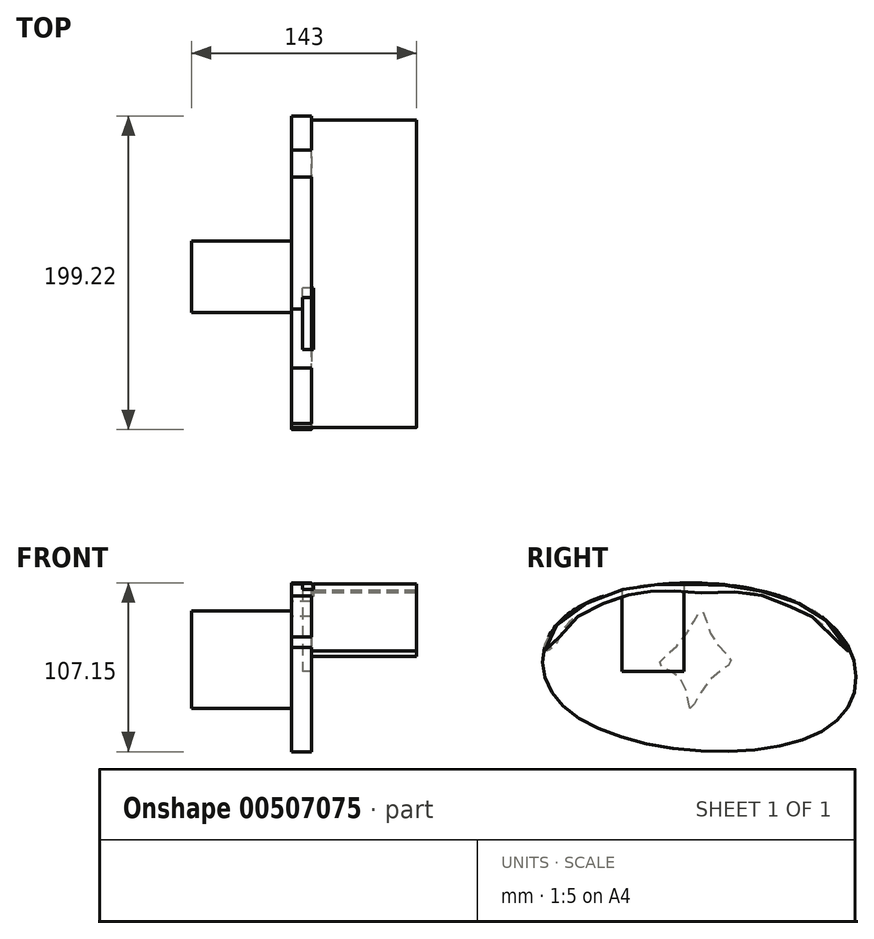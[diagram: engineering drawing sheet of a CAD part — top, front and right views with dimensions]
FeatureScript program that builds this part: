
annotation { "Feature Type Name" : "Feature", "Feature Type Description" : "" }
export const myFeature = defineFeature(function(context is Context, id is Id, definition is map)
    precondition{}
    {
        {
            var Q0;
            Q0=qCreatedBy(makeId("Right.planeOp"),FACE);
            var sketch = newSketch(context, id + "F0", { "sketchPlane" : qUnion([Q0])});
            skFitSpline(sketch, "E0", {"points": [v(-52.26, 26.74) * mm, v(-52.02, -34.24) * mm, v(116.31, -42.83) * mm, v(110.35, 24.54) * mm, v(-52.26, 26.74) * mm]});
            skSolve(sketch);
        }
        {
            var Q0;
            Q0=makeQuery(id+"F0.imprint","IMPRINT",FACE,{"disambiguationData":[TD([[makeQuery(id+"F0.imprint","IMPRINT",EDGE,{"derivedFrom":sQuery(id+"F0.wireOp",EDGE,"E0")}),1.0]])]});
            extrude(context, id + "F1", {"entities" : qUnion([Q0]), "depth" : 12.7 * mm});
        }
        {
            var Q0;
            Q0=qCreatedBy(makeId("Right.planeOp"),FACE);
            var sketch = newSketch(context, id + "F2", { "sketchPlane" : qUnion([Q0])});
            skFitSpline(sketch, "E1", {"points": [v(25.54, -32.86) * mm, v(20.23, -14.93) * mm, v(6.03, -4.9) * mm, v(20.25, 9.96) * mm, v(32.93, 29) * mm, v(40.33, 11.1) * mm, v(51.59, -3.17) * mm, v(38.82, -14.11) * mm, v(25.54, -32.86) * mm]});
            skSolve(sketch);
        }
        {
            var Q0;
            Q0=makeQuery(id+"F2.imprint","IMPRINT",FACE,{"disambiguationData":[TD([[makeQuery(id+"F2.imprint","IMPRINT",EDGE,{"derivedFrom":sQuery(id+"F2.wireOp",EDGE,"E1")}),-1.0]])]});
            extrude(context, id + "F3", {"entities" : qUnion([Q0]), "operationType" : NewBodyOperationType.ADD, "oppositeDirection" : true, "depth" : 63.75 * mm});
        }
        {
            var Q0;
            Q0=qCreatedBy(makeId("Top.planeOp"),FACE);
            var sketch = newSketch(context, id + "F4", { "sketchPlane" : qUnion([Q0])});
            skArc(sketch, "E2", {"start": v(13.62, -67.46) * mm, "mid": v(81.56, 31.79) * mm, "end": v(13.16, 130.71) * mm});
            skSolve(sketch);
        }
        {
            var Q0;
            Q0=sQuery(id+"F4.wireOp",EDGE,"E2");
            extrude(context, id + "F5", {"bodyType" : ToolBodyType.SURFACE, "surfaceEntities" : qUnion([Q0]), "oppositeDirection" : true, "depth" : 16 * mm});
        }
        {
            var Q0;
            Q0=qCreatedBy(makeId("Right.planeOp"),FACE);
            var sketch = newSketch(context, id + "F6", { "sketchPlane" : qUnion([Q0])});
            skFitSpline(sketch, "E3", {"points": [v(-66.68, 3.98) * mm, v(-60.7, 18) * mm, v(-37.08, 35.13) * mm, v(-7.37, 44.85) * mm, v(16.95, 45.89) * mm, v(41.56, 45.49) * mm, v(68.88, 41.75) * mm, v(98.43, 32.2) * mm, v(115.66, 18.57) * mm, v(128.15, 0) * mm, v(111.03, 18.78) * mm, v(96.84, 28.7) * mm, v(82.82, 34.34) * mm, v(63.83, 40.55) * mm, v(47.76, 40.57) * mm, v(23.87, 40.93) * mm, v(12.48, 41.8) * mm, v(0, 41.25) * mm, v(-10.09, 39.97) * mm, v(-24.19, 35.97) * mm, v(-38.05, 29.46) * mm, v(-53.49, 19.45) * mm, v(-60.85, 6.58) * mm, v(-66.68, 3.98) * mm]});
            skSolve(sketch);
        }
        {
            var Q0;
            Q0 = qSketchRegion(id + "F6", true);
            extrude(context, id + "F7", {"entities" : qUnion([Q0]), "operationType" : NewBodyOperationType.ADD, "depth" : 79.25 * mm});
        }
        {
            var Q0;
            Q0=qCreatedBy(makeId("Right.planeOp"),FACE);
            var sketch = newSketch(context, id + "F8", { "sketchPlane" : qUnion([Q0])});
            skLineSegment(sketch, "E4.bottom", {"start": v(-17.58, 46.45) * mm, "end": v(21.52, 46.45) * mm});
            skLineSegment(sketch, "E4.top", {"start": v(-17.58, -9.33) * mm, "end": v(21.52, -9.33) * mm});
            skLineSegment(sketch, "E4.left", {"start": v(-17.58, 46.45) * mm, "end": v(-17.58, -9.33) * mm});
            skLineSegment(sketch, "E4.right", {"start": v(21.52, 46.45) * mm, "end": v(21.52, -9.33) * mm});
            skSolve(sketch);
        }
        {
            var Q0;
            Q0 = qSketchRegion(id + "F8", true);
            extrude(context, id + "F9", {"entities" : qUnion([Q0]), "operationType" : NewBodyOperationType.REMOVE, "depth" : 13.97 * mm, "hasSecondDirection" : true, "secondDirectionOppositeDirection" : false, "secondDirectionDepth" : 6.86 * mm});
        }
    });
